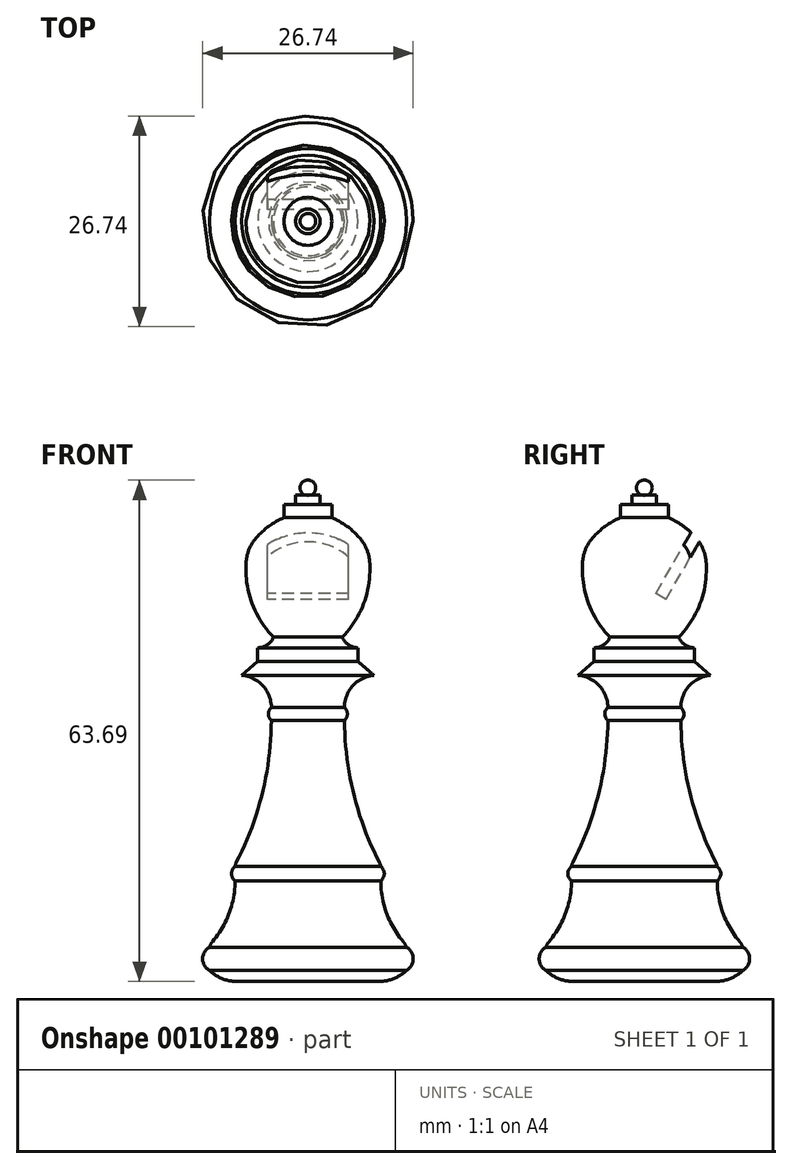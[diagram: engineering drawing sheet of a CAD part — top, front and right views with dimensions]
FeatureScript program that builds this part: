
annotation { "Feature Type Name" : "Feature", "Feature Type Description" : "" }
export const myFeature = defineFeature(function(context is Context, id is Id, definition is map)
    precondition{}
    {
        {
            var Q0;
            Q0=qCreatedBy(makeId("Front.planeOp"),FACE);
            var sketch = newSketch(context, id + "F0", { "sketchPlane" : qUnion([Q0])});
            skLineSegment(sketch, "E0", {"start": v(-100.9, 26.37) * mm, "end": v(-100.9, 27.76) * mm});
            skArc(sketch, "E1", {"start": v(-100.9, 27.76) * mm, "mid": v(-100.04, 29.24) * mm, "end": v(-100.9, 30.72) * mm});
            skLineSegment(sketch, "E2", {"start": v(-100.9, 30.72) * mm, "end": v(-100.9, 32.11) * mm});
            skLineSegment(sketch, "E3", {"start": v(-104.16, 39.17) * mm, "end": v(-104.16, 32.11) * mm});
            skLineSegment(sketch, "E4", {"start": v(-104.16, 32.11) * mm, "end": v(-100.9, 32.11) * mm});
            skArc(sketch, "E5", {"start": v(-104.16, 39.17) * mm, "mid": v(-103.7, 40.06) * mm, "end": v(-104.16, 40.96) * mm});
            skLineSegment(sketch, "E6", {"start": v(-104.16, 40.96) * mm, "end": v(-104.16, 42.27) * mm});
            skLineSegment(sketch, "E7", {"start": v(-108.77, 59.52) * mm, "end": v(-108.77, 42.27) * mm});
            skLineSegment(sketch, "E8", {"start": v(-108.77, 42.27) * mm, "end": v(-104.16, 42.27) * mm});
            skArc(sketch, "E9", {"start": v(-108.77, 59.52) * mm, "mid": v(-108.39, 60.34) * mm, "end": v(-108.77, 61.17) * mm});
            skLineSegment(sketch, "E10", {"start": v(-108.77, 61.17) * mm, "end": v(-108.77, 65.24) * mm});
            skLineSegment(sketch, "E11", {"start": v(-108.77, 65.24) * mm, "end": v(-105, 65.24) * mm});
            skLineSegment(sketch, "E12", {"start": v(-105, 65.24) * mm, "end": v(-107.04, 67) * mm});
            skLineSegment(sketch, "E13", {"start": v(-107.04, 67) * mm, "end": v(-107.04, 68.75) * mm});
            skLineSegment(sketch, "E14", {"start": v(-107.04, 68.75) * mm, "end": v(-109.04, 68.75) * mm});
            skLineSegment(sketch, "E15", {"start": v(-109.04, 68.75) * mm, "end": v(-109.04, 70.1) * mm});
            skLineSegment(sketch, "E16", {"start": v(-110.36, 85.28) * mm, "end": v(-110.36, 86.98) * mm});
            skLineSegment(sketch, "E17", {"start": v(-110.36, 86.98) * mm, "end": v(-111.85, 86.98) * mm});
            skLineSegment(sketch, "E18", {"start": v(-111.85, 86.98) * mm, "end": v(-111.85, 88.16) * mm});
            skLineSegment(sketch, "E19", {"start": v(-113.4, 88.16) * mm, "end": v(-111.85, 88.16) * mm});
            skLineSegment(sketch, "E20", {"start": v(-113.4, 88.16) * mm, "end": v(-113.4, 26.37) * mm});
            skLineSegment(sketch, "E21", {"start": v(-113.4, 26.37) * mm, "end": v(-100.9, 26.37) * mm});
            skArc(sketch, "E22", {"start": v(-105.78, 81.21) * mm, "mid": v(-107.74, 83.62) * mm, "end": v(-110.36, 85.28) * mm});
            skArc(sketch, "E23", {"start": v(-109.04, 70.1) * mm, "mid": v(-106.03, 75.25) * mm, "end": v(-105.78, 81.21) * mm});
            skSolve(sketch);
        }
        {
            var Q0;
            Q0=makeQuery(id+"F0.imprint","IMPRINT",FACE,{"disambiguationData":[TD([[makeQuery(id+"F0.imprint","IMPRINT",EDGE,{"derivedFrom":sQuery(id+"F0.wireOp",EDGE,"E0")}),1.0]])]});
            var Q1;
            Q1=sQuery(id+"F0.wireOp",EDGE,"E20");
            revolve(context, id + "F1", {"entities" : qUnion([Q0]), "axis" : qUnion([Q1]), "revolveType" : RevolveType.FULL});
        }
        {
            var Q0;
            Q0=makeQuery(id+"F1.opRevolve","SWEPT_EDGE",EDGE,{"disambiguationData":[OSD([sQuery(id+"F0.wireOp",EDGE,"E0"),sQuery(id+"F0.wireOp",EDGE,"E21")])]});
            fillet(context, id + "F2", {"entities" : qUnion([Q0]), "radius" : 5 * mm, "tangentPropagation" : true, "allowEdgeOverflow" : false});
        }
        {
            var Q0;
            Q0=makeQuery(id+"F1.opRevolve","SWEPT_EDGE",EDGE,{"disambiguationData":[OSD([sQuery(id+"F0.wireOp",EDGE,"E2"),sQuery(id+"F0.wireOp",EDGE,"E4")])]});
            fillet(context, id + "F3", {"entities" : qUnion([Q0]), "radius" : 2 * mm, "tangentPropagation" : true, "allowEdgeOverflow" : false});
        }
        {
            var Q0;
            Q0=makeQuery(id+"F1.opRevolve","SWEPT_EDGE",EDGE,{"disambiguationData":[OSD([sQuery(id+"F0.wireOp",EDGE,"E3"),sQuery(id+"F0.wireOp",EDGE,"E4")])]});
            fillet(context, id + "F4", {"entities" : qUnion([Q0]), "radius" : 12 * mm, "tangentPropagation" : true, "allowEdgeOverflow" : false});
        }
        {
            var Q0;
            Q0=makeQuery(id+"F1.opRevolve","SWEPT_EDGE",EDGE,{"disambiguationData":[OSD([sQuery(id+"F0.wireOp",EDGE,"E6"),sQuery(id+"F0.wireOp",EDGE,"E8")])]});
            fillet(context, id + "F5", {"entities" : qUnion([Q0]), "radius" : 1.5 * mm, "tangentPropagation" : true, "allowEdgeOverflow" : false});
        }
        {
            var Q0;
            Q0=makeQuery(id+"F1.opRevolve","SWEPT_EDGE",EDGE,{"disambiguationData":[OSD([sQuery(id+"F0.wireOp",EDGE,"E7"),sQuery(id+"F0.wireOp",EDGE,"E8")])]});
            fillet(context, id + "F6", {"entities" : qUnion([Q0]), "radius" : 40 * mm, "tangentPropagation" : true, "allowEdgeOverflow" : false});
        }
        {
            var Q0;
            Q0=makeQuery(id+"F1.opRevolve","SWEPT_EDGE",EDGE,{"disambiguationData":[OSD([sQuery(id+"F0.wireOp",EDGE,"E10"),sQuery(id+"F0.wireOp",EDGE,"E11")])]});
            fillet(context, id + "F7", {"entities" : qUnion([Q0]), "radius" : 4.08 * mm, "tangentPropagation" : true, "allowEdgeOverflow" : false});
        }
        {
            var Q0;
            Q0=makeQuery(id+"F1.opRevolve","SWEPT_EDGE",EDGE,{"disambiguationData":[OSD([sQuery(id+"F0.wireOp",EDGE,"E14"),sQuery(id+"F0.wireOp",EDGE,"E15")])]});
            fillet(context, id + "F8", {"entities" : qUnion([Q0]), "radius" : 2.14 * mm, "tangentPropagation" : true, "allowEdgeOverflow" : false});
        }
        {
            var Q0;
            Q0=makeQuery(id+"F1.opRevolve","SWEPT_FACE",FACE,{"disambiguationData":[OSD([sQuery(id+"F0.wireOp",EDGE,"E19")])]});
            cPlane(context, id + "F9", {"entities" : qUnion([Q0]), "cplaneType" : CPlaneType.OFFSET, "offset" : 0.1 * mm, "oppositeDirection" : true, "width" : 150 * mm, "height" : 150 * mm});
        }
        {
            var Q0;
            Q0=qCreatedBy(id+"F9.planeOp",FACE);
            var sketch = newSketch(context, id + "F10", { "sketchPlane" : qUnion([Q0])});
            skCircle(sketch, "E24", {"center": v(-113.4, 0) * mm, "radius": 1 * mm});
            skSolve(sketch);
        }
        {
            var Q0;
            Q0=makeQuery(id+"F10.imprint","IMPRINT",FACE,{"disambiguationData":[TD([[makeQuery(id+"F10.imprint","IMPRINT",EDGE,{"derivedFrom":sQuery(id+"F10.wireOp",EDGE,"E24")}),1.0]])]});
            extrude(context, id + "F11", {"entities" : qUnion([Q0]), "depth" : 2 * mm});
        }
        {
            var Q0;
            Q0=makeQuery(id+"F11.opExtrude","CAP_EDGE",EDGE,{"disambiguationData":[OSD([sQuery(id+"F10.wireOp",EDGE,"E24")])],"isStart":false});
            var Q1;
            Q1=makeQuery(id+"F11.opExtrude","CAP_EDGE",EDGE,{"disambiguationData":[OSD([sQuery(id+"F10.wireOp",EDGE,"E24")])],"isStart":true});
            fillet(context, id + "F12", {"entities" : qUnion([Q0, Q1]), "radius" : 1 * mm, "tangentPropagation" : true, "allowEdgeOverflow" : false});
        }
        {
            var Q0;
            Q0=makeQuery(id+"F1.opRevolve","SWEPT_EDGE",EDGE,{"disambiguationData":[OSD([sQuery(id+"F0.wireOp",EDGE,"E22"),sQuery(id+"F0.wireOp",EDGE,"E23")])]});
            fillet(context, id + "F13", {"entities" : qUnion([Q0]), "radius" : 5 * mm, "tangentPropagation" : true, "allowEdgeOverflow" : false});
        }
        {
            var Q0;
            Q0=qCreatedBy(id+"F9.planeOp",FACE);
            var sketch = newSketch(context, id + "F14", { "sketchPlane" : qUnion([Q0])});
            skLineSegment(sketch, "E25", {"start": v(-110.39, 0) * mm, "end": v(-116.55, 0) * mm});
            skSolve(sketch);
        }
        {
            var Q0;
            Q0=qCreatedBy(id+"F9.planeOp",FACE);
            var Q1;
            Q1=sQuery(id+"F14.wireOp",EDGE,"E25");
            cPlane(context, id + "F15", {"entities" : qUnion([Q0, Q1]), "cplaneType" : CPlaneType.LINE_ANGLE, "offset" : 1 * mm, "angle" : 30 * degree, "width" : 150 * mm, "height" : 150 * mm});
        }
        {
            var Q0;
            Q0=qCreatedBy(id+"F15.planeOp",FACE);
            var sketch = newSketch(context, id + "F16", { "sketchPlane" : qUnion([Q0])});
            skLineSegment(sketch, "E26.top", {"start": v(-108.26, 35.06) * mm, "end": v(-118.56, 35.06) * mm});
            skLineSegment(sketch, "E27.top", {"start": v(-108.26, 36.57) * mm, "end": v(-118.56, 36.57) * mm});
            skLineSegment(sketch, "E27.left", {"start": v(-108.26, 35.06) * mm, "end": v(-108.26, 36.57) * mm});
            skLineSegment(sketch, "E27.right", {"start": v(-118.56, 35.06) * mm, "end": v(-118.56, 36.57) * mm});
            skSolve(sketch);
        }
        {
            var Q0;
            Q0=makeQuery(id+"F16.imprint","IMPRINT",FACE,{"disambiguationData":[TD([[makeQuery(id+"F16.imprint","IMPRINT",EDGE,{"derivedFrom":sQuery(id+"F16.wireOp",EDGE,"E26.top")}),-1.0]])]});
            extrude(context, id + "F17", {"entities" : qUnion([Q0]), "operationType" : NewBodyOperationType.REMOVE, "depth" : 10 * mm});
        }
    });
